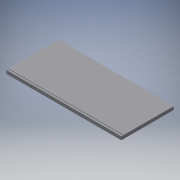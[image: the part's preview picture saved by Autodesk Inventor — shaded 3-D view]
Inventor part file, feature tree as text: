
AUTODESK INVENTOR PART (.ipt)
format: ipt  version: 2018.3 (Build 223284000, 284)  size: 111,616 bytes
history: native  units: mm
features: extrude x3, sketch x3
ambient origin geometry x8: Origin, YZ Plane, XZ Plane, XY Plane, X Axis, Y Axis, Z Axis, Center Point
bodies: Solid1 (feature_tree)
feature tree (6):
  extrude  "Extrusion1"  Depth=15.7mm
  extrude  "Extrusion3"  Depth=0.15mm
  extrude  "Extrusion4"  Depth=0.15mm TaperAngle=0.0deg
  sketch  "Sketch1"  dims[d0=34.5mm d1=15.7mm]
  sketch  "Sketch3"  dims[d2=1.0mm d3=0.0mm d8=0.15mm]
  sketch  "Sketch4"  dims[d9=0.3mm d10=7.0mm d11=0.0mm d12=0.4mm d13=0.1mm d14=0.15mm d15=0.0mm]
